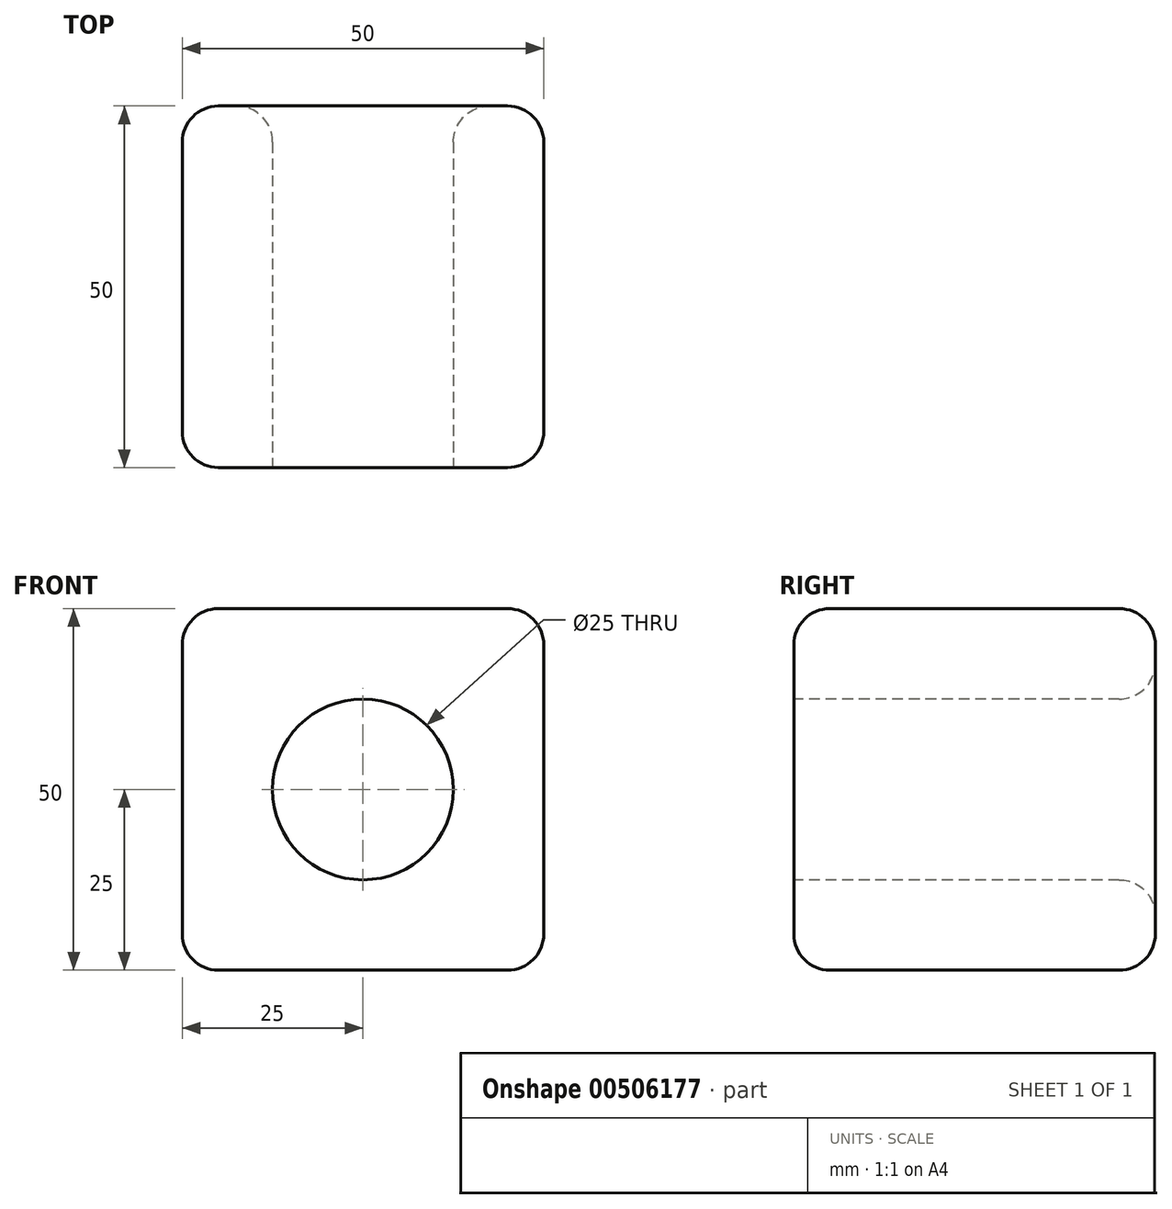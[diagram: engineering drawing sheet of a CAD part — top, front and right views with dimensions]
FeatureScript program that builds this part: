
annotation { "Feature Type Name" : "Feature", "Feature Type Description" : "" }
export const myFeature = defineFeature(function(context is Context, id is Id, definition is map)
    precondition{}
    {
        {
            var Q0;
            Q0=qCreatedBy(makeId("Top.planeOp"),FACE);
            var sketch = newSketch(context, id + "F0", { "sketchPlane" : qUnion([Q0])});
            skLineSegment(sketch, "E0.bottom", {"start": v(25, -25) * mm, "end": v(-25, -25) * mm});
            skLineSegment(sketch, "E0.top", {"start": v(25, 25) * mm, "end": v(-25, 25) * mm});
            skLineSegment(sketch, "E0.left", {"start": v(25, -25) * mm, "end": v(25, 25) * mm});
            skLineSegment(sketch, "E0.right", {"start": v(-25, -25) * mm, "end": v(-25, 25) * mm});
            skPoint(sketch, "E0.middle", {"position": v(0, 0) * mm});
            skSolve(sketch);
        }
        {
            var Q0;
            Q0 = qSketchRegion(id + "F0", true);
            extrude(context, id + "F1", {"entities" : qUnion([Q0]), "depth" : 50 * mm});
        }
        {
            var Q0;
            Q0=makeQuery(id+"F1.opExtrude","SWEPT_FACE",FACE,{"disambiguationData":[OSD([sQuery(id+"F0.wireOp",EDGE,"E0.bottom")])]});
            var sketch = newSketch(context, id + "F2", { "sketchPlane" : qUnion([Q0])});
            skCircle(sketch, "E1", {"center": v(0, 25) * mm, "radius": 12.5 * mm});
            skSolve(sketch);
        }
        {
            var Q0;
            Q0 = qSketchRegion(id + "F2", true);
            extrude(context, id + "F3", {"entities" : qUnion([Q0]), "operationType" : NewBodyOperationType.REMOVE, "endBound" : BoundingType.THROUGH_ALL, "oppositeDirection" : true, "depth" : 25 * mm});
        }
        {
            var Q0;
            Q0=makeQuery(id+"F1.opExtrude","CAP_EDGE",EDGE,{"disambiguationData":[OSD([sQuery(id+"F0.wireOp",EDGE,"E0.bottom")])],"isStart":false});
            var Q1;
            Q1=makeQuery(id+"F1.opExtrude","CAP_EDGE",EDGE,{"disambiguationData":[OSD([sQuery(id+"F0.wireOp",EDGE,"E0.right")])],"isStart":false});
            var Q2;
            Q2=makeQuery(id+"F1.opExtrude","CAP_EDGE",EDGE,{"disambiguationData":[OSD([sQuery(id+"F0.wireOp",EDGE,"E0.top")])],"isStart":false});
            var Q3;
            Q3=makeQuery(id+"F1.opExtrude","CAP_EDGE",EDGE,{"disambiguationData":[OSD([sQuery(id+"F0.wireOp",EDGE,"E0.left")])],"isStart":false});
            var Q4;
            Q4=makeQuery(id+"F1.opExtrude","SWEPT_EDGE",EDGE,{"disambiguationData":[OSD([sQuery(id+"F0.wireOp",EDGE,"E0.top"),sQuery(id+"F0.wireOp",EDGE,"E0.left")])]});
            var Q5;
            Q5=makeQuery(id+"F1.opExtrude","SWEPT_EDGE",EDGE,{"disambiguationData":[OSD([sQuery(id+"F0.wireOp",EDGE,"E0.bottom"),sQuery(id+"F0.wireOp",EDGE,"E0.left")])]});
            var Q6;
            Q6=makeQuery(id+"F1.opExtrude","CAP_EDGE",EDGE,{"disambiguationData":[OSD([sQuery(id+"F0.wireOp",EDGE,"E0.left")])],"isStart":true});
            var Q7;
            Q7=makeQuery(id+"F1.opExtrude","CAP_EDGE",EDGE,{"disambiguationData":[OSD([sQuery(id+"F0.wireOp",EDGE,"E0.bottom")])],"isStart":true});
            var Q8;
            Q8=makeQuery(id+"F1.opExtrude","SWEPT_EDGE",EDGE,{"disambiguationData":[OSD([sQuery(id+"F0.wireOp",EDGE,"E0.bottom"),sQuery(id+"F0.wireOp",EDGE,"E0.right")])]});
            var Q9;
            Q9=makeQuery(id+"F1.opExtrude","CAP_EDGE",EDGE,{"disambiguationData":[OSD([sQuery(id+"F0.wireOp",EDGE,"E0.right")])],"isStart":true});
            var Q10;
            Q10=makeQuery(id+"F1.opExtrude","CAP_EDGE",EDGE,{"disambiguationData":[OSD([sQuery(id+"F0.wireOp",EDGE,"E0.top")])],"isStart":true});
            var Q11;
            Q11=makeQuery(id+"F1.opExtrude","SWEPT_EDGE",EDGE,{"disambiguationData":[OSD([sQuery(id+"F0.wireOp",EDGE,"E0.top"),sQuery(id+"F0.wireOp",EDGE,"E0.right")])]});
            fillet(context, id + "F4", {"entities" : qUnion([Q0, Q1, Q2, Q3, Q4, Q5, Q6, Q7, Q8, Q9, Q10, Q11]), "radius" : 5 * mm, "tangentPropagation" : true, "allowEdgeOverflow" : false});
        }
        {
            var Q0;
            Q0=makeQuery(id+"F3.boolean.opBoolean","COPY",EDGE,{"derivedFrom":makeQuery(id+"F3.opExtrude","CAP_EDGE",EDGE,{"disambiguationData":[OSD([sQuery(id+"F2.wireOp",EDGE,"E1")])],"isStart":true})});
            var Q1;
            {var subQ0=sQuery(id+"F0.wireOp",EDGE,"E0.left");Q1=makeQuery(id+"F4.opFillet","BLEND_EDGE",EDGE,{"blendedFrom":[makeQuery(id+"F1.opExtrude","CAP_VERTEX",VERTEX,{"disambiguationData":[OSD([sQuery(id+"F0.wireOp",EDGE,"E0.top"),subQ0])],"isStart":true}),makeQuery(id+"F1.opExtrude","CAP_EDGE",EDGE,{"disambiguationData":[OSD([subQ0])],"isStart":true})],"blendedInto":[]});}
            var Q2;
            {var subQ0=sQuery(id+"F0.wireOp",EDGE,"E0.left");Q2=makeQuery(id+"F4.opFillet","BLEND_EDGE",EDGE,{"blendedFrom":[makeQuery(id+"F1.opExtrude","CAP_EDGE",EDGE,{"disambiguationData":[OSD([subQ0])],"isStart":true}),makeQuery(id+"F1.opExtrude","SWEPT_FACE",FACE,{"disambiguationData":[OSD([subQ0])]})],"blendedInto":[makeQuery(id+"F1.opExtrude","SWEPT_FACE",FACE,{"disambiguationData":[OSD([subQ0])]})]});}
            var Q3;
            {var subQ0=sQuery(id+"F0.wireOp",EDGE,"E0.left");Q3=makeQuery(id+"F4.opFillet","BLEND_EDGE",EDGE,{"blendedFrom":[makeQuery(id+"F1.opExtrude","CAP_EDGE",EDGE,{"disambiguationData":[OSD([subQ0])],"isStart":true}),makeQuery(id+"F1.opExtrude","CAP_FACE",FACE,{"disambiguationData":[OSD([sQuery(id+"F0.wireOp",EDGE,"E0.bottom"),sQuery(id+"F0.wireOp",EDGE,"E0.top"),subQ0,sQuery(id+"F0.wireOp",EDGE,"E0.right")])],"isStart":true})],"blendedInto":[makeQuery(id+"F1.opExtrude","CAP_FACE",FACE,{"disambiguationData":[OSD([sQuery(id+"F0.wireOp",EDGE,"E0.bottom"),sQuery(id+"F0.wireOp",EDGE,"E0.top"),subQ0,sQuery(id+"F0.wireOp",EDGE,"E0.right")])],"isStart":true})]});}
            var Q4;
            {var subQ0=sQuery(id+"F0.wireOp",EDGE,"E0.top");Q4=makeQuery(id+"F4.opFillet","BLEND_EDGE",EDGE,{"blendedFrom":[makeQuery(id+"F1.opExtrude","CAP_EDGE",EDGE,{"disambiguationData":[OSD([subQ0])],"isStart":true}),makeQuery(id+"F1.opExtrude","CAP_FACE",FACE,{"disambiguationData":[OSD([sQuery(id+"F0.wireOp",EDGE,"E0.bottom"),subQ0,sQuery(id+"F0.wireOp",EDGE,"E0.left"),sQuery(id+"F0.wireOp",EDGE,"E0.right")])],"isStart":true})],"blendedInto":[makeQuery(id+"F1.opExtrude","CAP_FACE",FACE,{"disambiguationData":[OSD([sQuery(id+"F0.wireOp",EDGE,"E0.bottom"),subQ0,sQuery(id+"F0.wireOp",EDGE,"E0.left"),sQuery(id+"F0.wireOp",EDGE,"E0.right")])],"isStart":true})]});}
            var Q5;
            {var subQ0=sQuery(id+"F0.wireOp",EDGE,"E0.top");Q5=makeQuery(id+"F4.opFillet","BLEND_EDGE",EDGE,{"blendedFrom":[makeQuery(id+"F1.opExtrude","CAP_VERTEX",VERTEX,{"disambiguationData":[OSD([subQ0,sQuery(id+"F0.wireOp",EDGE,"E0.left")])],"isStart":true}),makeQuery(id+"F1.opExtrude","CAP_EDGE",EDGE,{"disambiguationData":[OSD([subQ0])],"isStart":true})],"blendedInto":[]});}
            var Q6;
            Q6=makeQuery(id+"F3.boolean.opBoolean","INTERSECT",EDGE,{"derivedFrom":[makeQuery(id+"F1.opExtrude","SWEPT_FACE",FACE,{"disambiguationData":[OSD([sQuery(id+"F0.wireOp",EDGE,"E0.top")])]}),makeQuery(id+"F3.opExtrude","SWEPT_FACE",FACE,{"disambiguationData":[OSD([sQuery(id+"F2.wireOp",EDGE,"E1")])]})]});
            fillet(context, id + "F5", {"entities" : qUnion([Q0, Q1, Q2, Q3, Q4, Q5, Q6]), "radius" : 5 * mm, "tangentPropagation" : true, "allowEdgeOverflow" : false});
        }
    });
